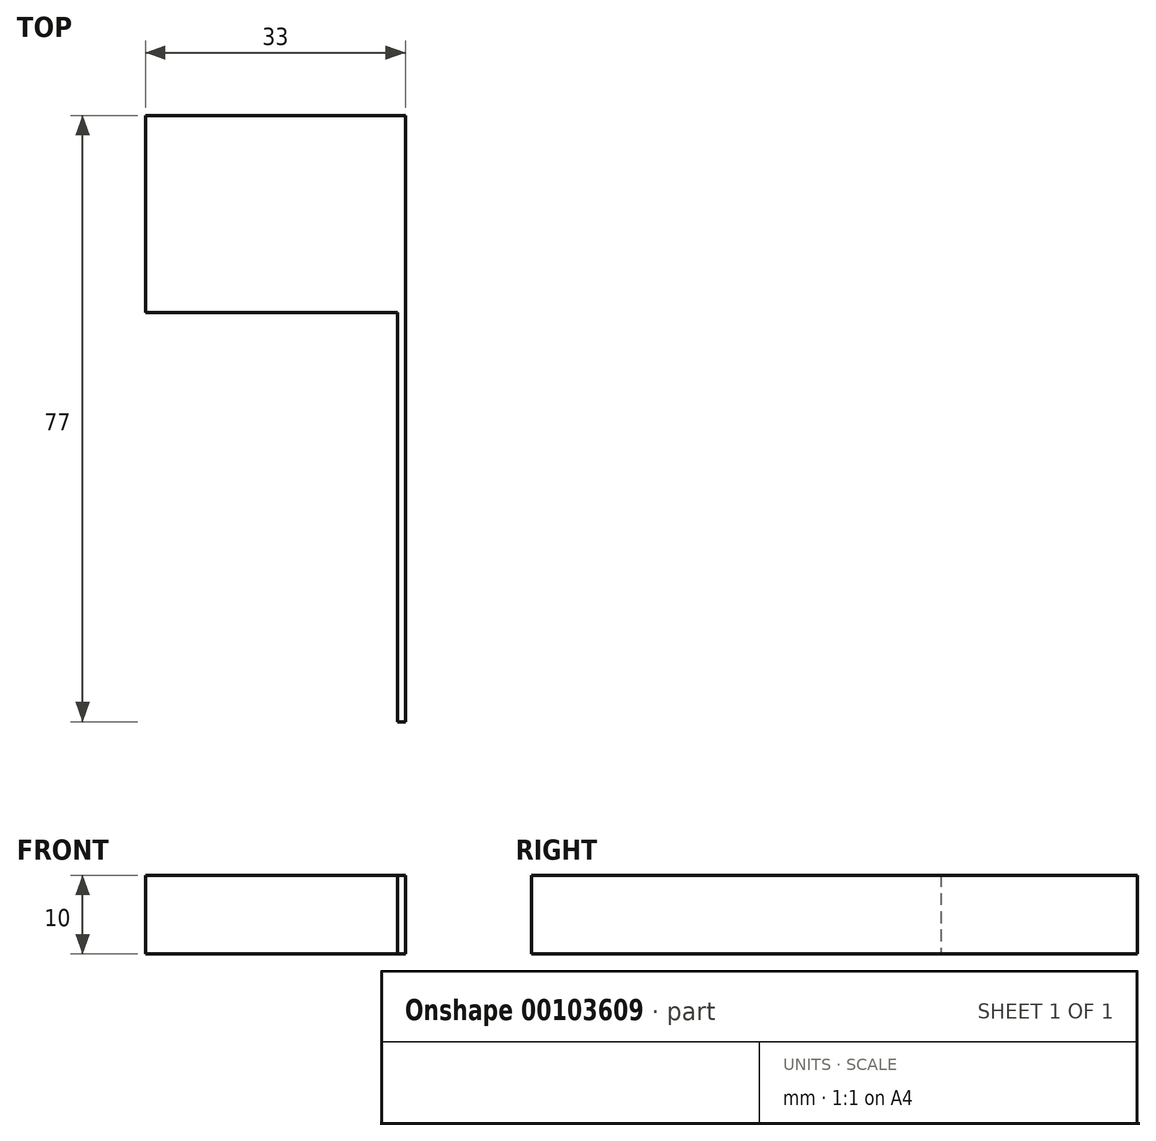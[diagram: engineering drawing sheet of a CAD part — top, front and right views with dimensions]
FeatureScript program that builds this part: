
annotation { "Feature Type Name" : "Feature", "Feature Type Description" : "" }
export const myFeature = defineFeature(function(context is Context, id is Id, definition is map)
    precondition{}
    {
        {
            var Q0;
            Q0=qCreatedBy(makeId("Front.planeOp"),FACE);
            var sketch = newSketch(context, id + "F0", { "sketchPlane" : qUnion([Q0])});
            skLineSegment(sketch, "E0.bottom", {"start": v(-20.6, 7.85) * mm, "end": v(11.4, 7.85) * mm});
            skLineSegment(sketch, "E0.top", {"start": v(-20.6, -2.15) * mm, "end": v(11.4, -2.15) * mm});
            skLineSegment(sketch, "E0.left", {"start": v(-20.6, 7.85) * mm, "end": v(-20.6, -2.15) * mm});
            skLineSegment(sketch, "E0.right", {"start": v(11.4, 7.85) * mm, "end": v(11.4, -2.15) * mm});
            skSolve(sketch);
        }
        {
            var Q0;
            Q0=makeQuery(id+"F0.imprint","IMPRINT",FACE,{"disambiguationData":[TD([[makeQuery(id+"F0.imprint","IMPRINT",EDGE,{"derivedFrom":sQuery(id+"F0.wireOp",EDGE,"E0.bottom")}),-1.0]])]});
            extrude(context, id + "F1", {"entities" : qUnion([Q0]), "depth" : 25 * mm});
        }
        {
            var Q0;
            Q0=makeQuery(id+"F1.opExtrude","SWEPT_FACE",FACE,{"disambiguationData":[OSD([sQuery(id+"F0.wireOp",EDGE,"E0.right")])]});
            var sketch = newSketch(context, id + "F2", { "sketchPlane" : qUnion([Q0])});
            skLineSegment(sketch, "E1.bottom", {"start": v(0, 7.85) * mm, "end": v(-77, 7.85) * mm});
            skLineSegment(sketch, "E1.top", {"start": v(0, -2.15) * mm, "end": v(-77, -2.15) * mm});
            skLineSegment(sketch, "E1.left", {"start": v(0, 7.85) * mm, "end": v(0, -2.15) * mm});
            skLineSegment(sketch, "E1.right", {"start": v(-77, 7.85) * mm, "end": v(-77, -2.15) * mm});
            skSolve(sketch);
        }
        {
            var Q0;
            {var subQ2=sQuery(id+"F2.wireOp",EDGE,"E1.right");Q0=makeQuery(id+"F2.imprint","IMPRINT",FACE,{"disambiguationData":[TD([[makeQuery(id+"F2.imprint","IMPRINT",EDGE,{"derivedFrom":subQ2}),1.0]])]});}
            var Q1;
            {var subQ0=sQuery(id+"F2.wireOp",EDGE,"E1.left");Q1=makeQuery(id+"F2.imprint","IMPRINT",FACE,{"disambiguationData":[TD([[makeQuery(id+"F2.imprint","IMPRINT",EDGE,{"derivedFrom":subQ0}),-1.0]])]});}
            extrude(context, id + "F3", {"entities" : qUnion([Q0, Q1]), "operationType" : NewBodyOperationType.ADD, "depth" : 1 * mm});
        }
    });
